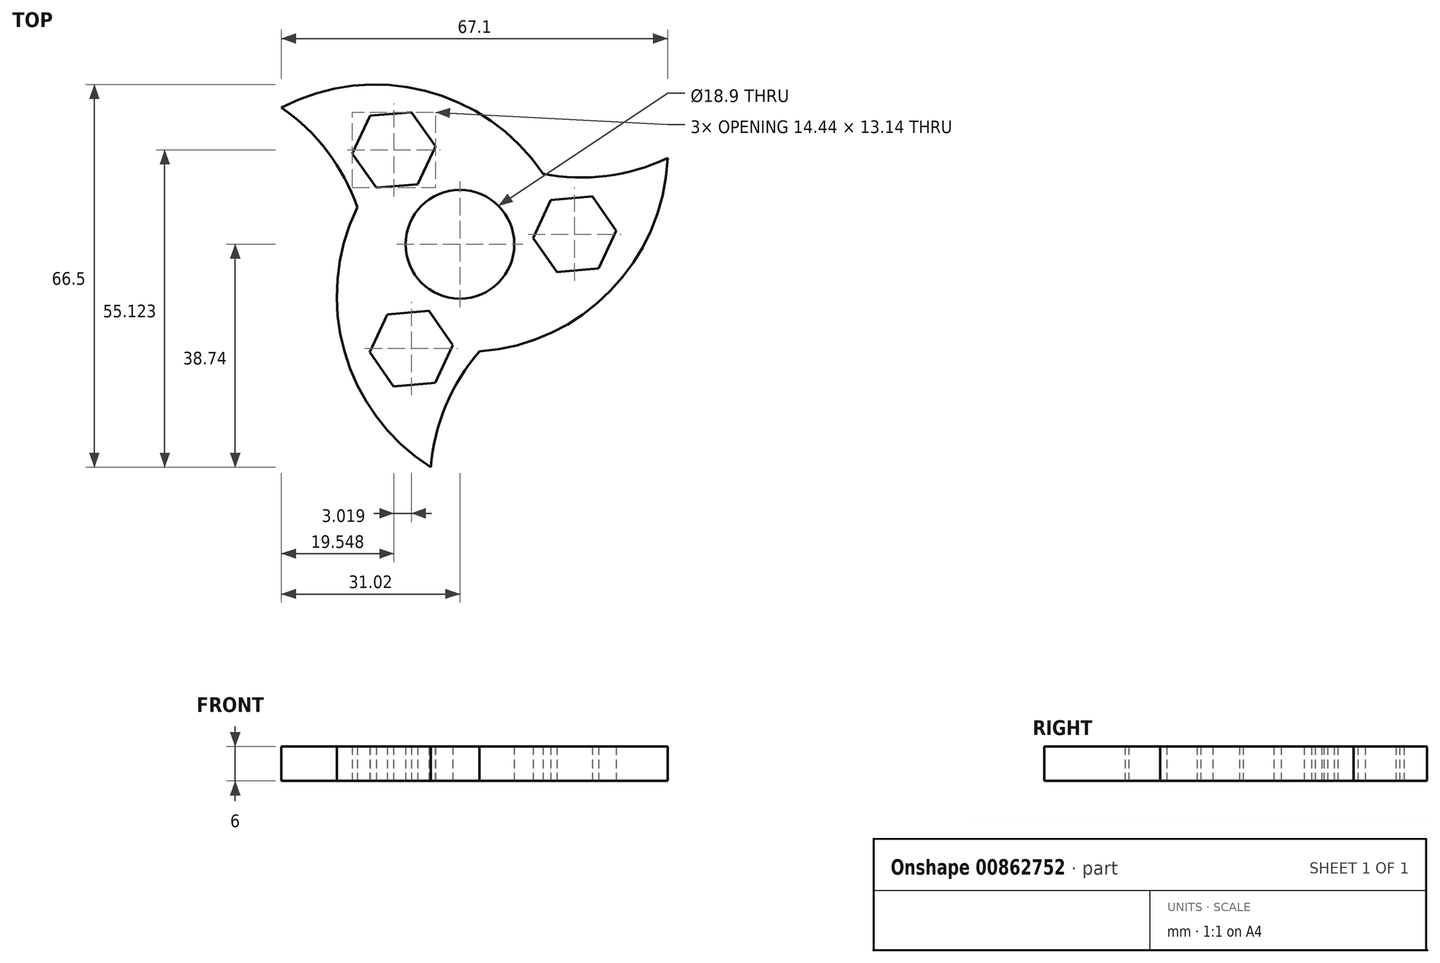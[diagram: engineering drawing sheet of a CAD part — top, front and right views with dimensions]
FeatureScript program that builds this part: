
annotation { "Feature Type Name" : "Feature", "Feature Type Description" : "" }
export const myFeature = defineFeature(function(context is Context, id is Id, definition is map)
    precondition{}
    {
        {
            var Q0;
            Q0=qCreatedBy(makeId("Top.planeOp"),FACE);
            var sketch = newSketch(context, id + "F0", { "sketchPlane" : qUnion([Q0])});
            skCircle(sketch, "E0", {"center": v(0, 0) * mm, "radius": 9.45 * mm});
            skPoint(sketch, "E1", {"position": v(0, 18.7) * mm});
            skPoint(sketch, "E2.MirrorP", {"position": v(0, -18.7) * mm});
            skArc(sketch, "E3", {"start": v(0, 18.7) * mm, "mid": v(17.52, 11.78) * mm, "end": v(36.08, 14.98) * mm});
            skArc(sketch, "E4", {"start": v(0, -18.7) * mm, "mid": v(24.95, -9.25) * mm, "end": v(36.08, 14.98) * mm});
            skArc(sketch, "E5.1.0", {"start": v(-16.19, -9.35) * mm, "mid": v(-18.96, 9.29) * mm, "end": v(-31.02, 23.76) * mm});
            skArc(sketch, "E5.1.1", {"start": v(16.19, 9.35) * mm, "mid": v(-4.46, 26.23) * mm, "end": v(-31.02, 23.76) * mm});
            skArc(sketch, "E5.2.0", {"start": v(16.19, -9.35) * mm, "mid": v(1.44, -21.06) * mm, "end": v(-5.07, -38.74) * mm});
            skArc(sketch, "E5.2.1", {"start": v(-16.19, 9.35) * mm, "mid": v(-20.49, -16.98) * mm, "end": v(-5.07, -38.74) * mm});
            skLineSegment(sketch, "E6", {"start": v(0, 0) * mm, "end": v(19.92, 1.74) * mm, "construction": true});
            skCircle(sketch, "E7.cCircle", {"center": v(19.92, 1.74) * mm, "radius": 7.25 * mm, "construction": true});
            skLineSegment(sketch, "E7.0", {"start": v(12.7, 1.11) * mm, "end": v(15.77, 7.68) * mm});
            skLineSegment(sketch, "E7.1", {"start": v(15.77, 7.68) * mm, "end": v(22.99, 8.31) * mm});
            skLineSegment(sketch, "E7.2", {"start": v(22.99, 8.31) * mm, "end": v(27.15, 2.37) * mm});
            skLineSegment(sketch, "E7.3", {"start": v(27.15, 2.37) * mm, "end": v(24.08, -4.2) * mm});
            skLineSegment(sketch, "E7.4", {"start": v(24.08, -4.2) * mm, "end": v(16.86, -4.83) * mm});
            skLineSegment(sketch, "E7.5", {"start": v(16.86, -4.83) * mm, "end": v(12.7, 1.11) * mm});
            skLineSegment(sketch, "E8.1.0", {"start": v(-14.54, 9.81) * mm, "end": v(-18.7, 15.75) * mm});
            skLineSegment(sketch, "E8.1.1", {"start": v(-18.7, 15.75) * mm, "end": v(-15.63, 22.32) * mm});
            skLineSegment(sketch, "E8.1.2", {"start": v(-15.63, 22.32) * mm, "end": v(-8.4, 22.95) * mm});
            skLineSegment(sketch, "E8.1.3", {"start": v(-8.4, 22.95) * mm, "end": v(-4.25, 17.01) * mm});
            skLineSegment(sketch, "E8.1.4", {"start": v(-4.25, 17.01) * mm, "end": v(-7.31, 10.44) * mm});
            skLineSegment(sketch, "E8.1.5", {"start": v(-7.31, 10.44) * mm, "end": v(-14.54, 9.81) * mm});
            skLineSegment(sketch, "E8.2.0", {"start": v(-1.23, -17.5) * mm, "end": v(-4.3, -24.07) * mm});
            skLineSegment(sketch, "E8.2.1", {"start": v(-4.3, -24.07) * mm, "end": v(-11.52, -24.7) * mm});
            skLineSegment(sketch, "E8.2.2", {"start": v(-11.52, -24.7) * mm, "end": v(-15.67, -18.76) * mm});
            skLineSegment(sketch, "E8.2.3", {"start": v(-15.67, -18.76) * mm, "end": v(-12.61, -12.19) * mm});
            skLineSegment(sketch, "E8.2.4", {"start": v(-12.61, -12.19) * mm, "end": v(-5.39, -11.56) * mm});
            skLineSegment(sketch, "E8.2.5", {"start": v(-5.39, -11.56) * mm, "end": v(-1.23, -17.5) * mm});
            skSolve(sketch);
        }
        {
            var Q0;
            Q0=makeQuery(id+"F0.imprint","IMPRINT",FACE,{"disambiguationData":[TD([[makeQuery(id+"F0.imprint","IMPRINT",EDGE,{"derivedFrom":sQuery(id+"F0.wireOp",EDGE,"E0")}),-1.0]])]});
            extrude(context, id + "F1", {"entities" : qUnion([Q0]), "depth" : 6 * mm, "offsetDistance" : 25 * mm});
        }
    });
